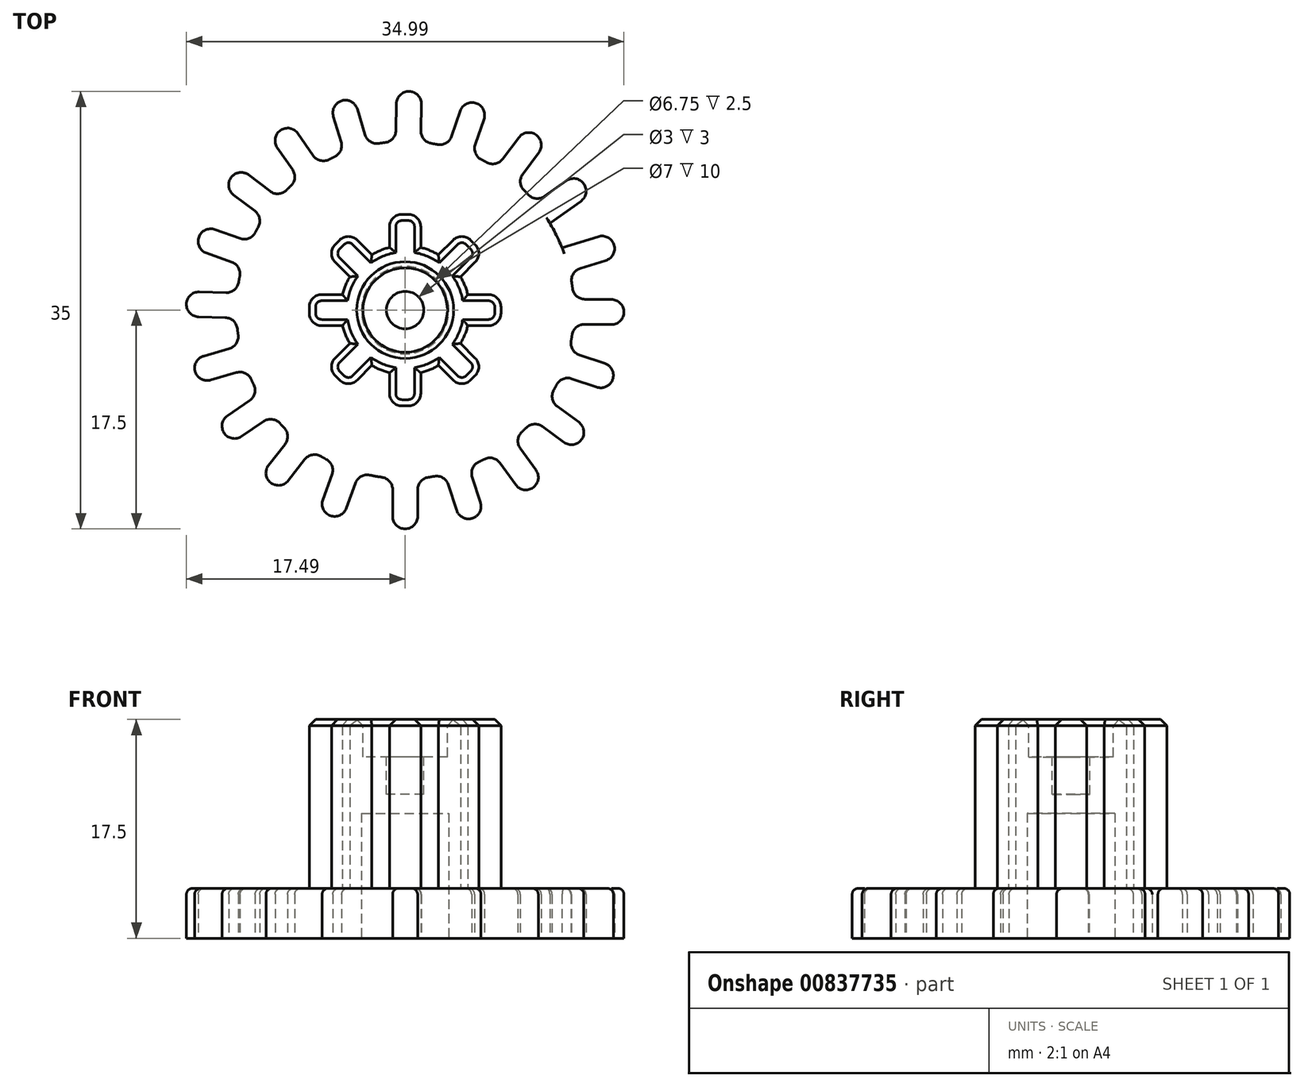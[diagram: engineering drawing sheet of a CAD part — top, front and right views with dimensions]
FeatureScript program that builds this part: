
annotation { "Feature Type Name" : "Feature", "Feature Type Description" : "" }
export const myFeature = defineFeature(function(context is Context, id is Id, definition is map)
    precondition{}
    {
        {
            var Q0;
            Q0=qCreatedBy(makeId("Top.planeOp"),FACE);
            var sketch = newSketch(context, id + "F0", { "sketchPlane" : qUnion([Q0])});
            skCircle(sketch, "E0", {"center": v(0, 0) * mm, "radius": 13.5 * mm});
            skSolve(sketch);
        }
        {
            var Q0;
            Q0 = qSketchRegion(id + "F0", true);
            extrude(context, id + "F1", {"entities" : qUnion([Q0]), "depth" : 4 * mm, "offsetDistance" : 25 * mm});
        }
        {
            var Q0;
            Q0=makeQuery(id+"F1.opExtrude","CAP_FACE",FACE,{"disambiguationData":[OSD([sQuery(id+"F0.wireOp",EDGE,"E0")])],"isStart":true});
            var sketch = newSketch(context, id + "F2", { "sketchPlane" : qUnion([Q0])});
            skCircle(sketch, "E1", {"center": v(0, 0) * mm, "radius": 5.17 * mm});
            skSolve(sketch);
        }
        {
            var Q0;
            Q0 = qSketchRegion(id + "F2", true);
            extrude(context, id + "F3", {"entities" : qUnion([Q0]), "operationType" : NewBodyOperationType.ADD, "oppositeDirection" : true, "depth" : 17.5 * mm, "offsetDistance" : 25 * mm});
        }
        {
            var Q0;
            Q0=makeQuery(id+"F1.opExtrude","CAP_FACE",FACE,{"disambiguationData":[OSD([sQuery(id+"F0.wireOp",EDGE,"E0")])],"isStart":true});
            var sketch = newSketch(context, id + "F4", { "sketchPlane" : qUnion([Q0])});
            skCircle(sketch, "E2", {"center": v(0, 0) * mm, "radius": 13.5 * mm});
            skLineSegment(sketch, "E3.bottom", {"start": v(1, 17.5) * mm, "end": v(-1, 17.5) * mm});
            skLineSegment(sketch, "E3.top", {"start": v(1, 9) * mm, "end": v(-1, 9) * mm});
            skLineSegment(sketch, "E3.left", {"start": v(1, 17.5) * mm, "end": v(1, 9) * mm});
            skLineSegment(sketch, "E3.right", {"start": v(-1, 17.5) * mm, "end": v(-1, 9) * mm});
            skPoint(sketch, "E3.middle", {"position": v(0, 13.25) * mm});
            skLineSegment(sketch, "E4.1.0", {"start": v(6.33, 16.35) * mm, "end": v(4.43, 16.96) * mm});
            skLineSegment(sketch, "E4.1.1", {"start": v(3.72, 8.26) * mm, "end": v(1.81, 8.87) * mm});
            skLineSegment(sketch, "E4.1.2", {"start": v(6.33, 16.35) * mm, "end": v(3.72, 8.26) * mm});
            skLineSegment(sketch, "E4.1.3", {"start": v(4.43, 16.96) * mm, "end": v(1.81, 8.87) * mm});
            skPoint(sketch, "E4.1.4", {"position": v(4.07, 12.6) * mm});
            skLineSegment(sketch, "E4.2.0", {"start": v(11.05, 13.61) * mm, "end": v(9.42, 14.78) * mm});
            skLineSegment(sketch, "E4.2.1", {"start": v(6.07, 6.72) * mm, "end": v(4.45, 7.89) * mm});
            skLineSegment(sketch, "E4.2.2", {"start": v(11.05, 13.61) * mm, "end": v(6.07, 6.72) * mm});
            skLineSegment(sketch, "E4.2.3", {"start": v(9.42, 14.78) * mm, "end": v(4.45, 7.89) * mm});
            skPoint(sketch, "E4.2.4", {"position": v(7.75, 10.75) * mm});
            skLineSegment(sketch, "E4.3.0", {"start": v(14.7, 9.56) * mm, "end": v(13.5, 11.17) * mm});
            skLineSegment(sketch, "E4.3.1", {"start": v(7.84, 4.52) * mm, "end": v(6.66, 6.14) * mm});
            skLineSegment(sketch, "E4.3.2", {"start": v(14.7, 9.56) * mm, "end": v(7.84, 4.52) * mm});
            skLineSegment(sketch, "E4.3.3", {"start": v(13.5, 11.17) * mm, "end": v(6.66, 6.14) * mm});
            skPoint(sketch, "E4.3.4", {"position": v(10.68, 7.85) * mm});
            skLineSegment(sketch, "E4.4.0", {"start": v(16.92, 4.58) * mm, "end": v(16.29, 6.48) * mm});
            skLineSegment(sketch, "E4.4.1", {"start": v(8.85, 1.9) * mm, "end": v(8.22, 3.8) * mm});
            skLineSegment(sketch, "E4.4.2", {"start": v(16.92, 4.58) * mm, "end": v(8.85, 1.9) * mm});
            skLineSegment(sketch, "E4.4.3", {"start": v(16.29, 6.48) * mm, "end": v(8.22, 3.8) * mm});
            skPoint(sketch, "E4.4.4", {"position": v(12.57, 4.19) * mm});
            skLineSegment(sketch, "E4.5.0", {"start": v(17.5, -0.84) * mm, "end": v(17.5, 1.16) * mm});
            skLineSegment(sketch, "E4.5.1", {"start": v(9, -0.92) * mm, "end": v(9, 1.08) * mm});
            skLineSegment(sketch, "E4.5.2", {"start": v(17.5, -0.84) * mm, "end": v(9, -0.92) * mm});
            skLineSegment(sketch, "E4.5.3", {"start": v(17.5, 1.16) * mm, "end": v(9, 1.08) * mm});
            skPoint(sketch, "E4.5.4", {"position": v(13.25, 0.12) * mm});
            skLineSegment(sketch, "E4.6.0", {"start": v(16.4, -6.18) * mm, "end": v(17, -4.27) * mm});
            skLineSegment(sketch, "E4.6.1", {"start": v(8.3, -3.64) * mm, "end": v(8.89, -1.73) * mm});
            skLineSegment(sketch, "E4.6.2", {"start": v(16.4, -6.18) * mm, "end": v(8.3, -3.64) * mm});
            skLineSegment(sketch, "E4.6.3", {"start": v(17, -4.27) * mm, "end": v(8.89, -1.73) * mm});
            skPoint(sketch, "E4.6.4", {"position": v(12.65, -3.96) * mm});
            skLineSegment(sketch, "E4.7.0", {"start": v(13.71, -10.92) * mm, "end": v(14.87, -9.29) * mm});
            skLineSegment(sketch, "E4.7.1", {"start": v(6.77, -6.01) * mm, "end": v(7.93, -4.38) * mm});
            skLineSegment(sketch, "E4.7.2", {"start": v(13.71, -10.92) * mm, "end": v(6.77, -6.01) * mm});
            skLineSegment(sketch, "E4.7.3", {"start": v(14.87, -9.29) * mm, "end": v(7.93, -4.38) * mm});
            skPoint(sketch, "E4.7.4", {"position": v(10.82, -7.65) * mm});
            skLineSegment(sketch, "E4.8.0", {"start": v(9.7, -14.6) * mm, "end": v(11.3, -13.4) * mm});
            skLineSegment(sketch, "E4.8.1", {"start": v(4.6, -7.8) * mm, "end": v(6.2, -6.6) * mm});
            skLineSegment(sketch, "E4.8.2", {"start": v(9.7, -14.6) * mm, "end": v(4.6, -7.8) * mm});
            skLineSegment(sketch, "E4.8.3", {"start": v(11.3, -13.4) * mm, "end": v(6.2, -6.6) * mm});
            skPoint(sketch, "E4.8.4", {"position": v(7.94, -10.6) * mm});
            skLineSegment(sketch, "E4.9.0", {"start": v(4.74, -16.88) * mm, "end": v(6.63, -16.23) * mm});
            skLineSegment(sketch, "E4.9.1", {"start": v(1.98, -8.84) * mm, "end": v(3.87, -8.19) * mm});
            skLineSegment(sketch, "E4.9.2", {"start": v(4.74, -16.88) * mm, "end": v(1.98, -8.84) * mm});
            skLineSegment(sketch, "E4.9.3", {"start": v(6.63, -16.23) * mm, "end": v(3.87, -8.19) * mm});
            skPoint(sketch, "E4.9.4", {"position": v(4.3, -12.53) * mm});
            skLineSegment(sketch, "E4.10.0", {"start": v(-0.68, -17.52) * mm, "end": v(1.32, -17.48) * mm});
            skLineSegment(sketch, "E4.10.1", {"start": v(-0.83, -9.02) * mm, "end": v(1.17, -8.98) * mm});
            skLineSegment(sketch, "E4.10.2", {"start": v(-0.68, -17.52) * mm, "end": v(-0.83, -9.02) * mm});
            skLineSegment(sketch, "E4.10.3", {"start": v(1.32, -17.48) * mm, "end": v(1.17, -8.98) * mm});
            skPoint(sketch, "E4.10.4", {"position": v(0.24, -13.25) * mm});
            skLineSegment(sketch, "E4.11.0", {"start": v(-6.03, -16.46) * mm, "end": v(-4.11, -17.04) * mm});
            skLineSegment(sketch, "E4.11.1", {"start": v(-3.56, -8.32) * mm, "end": v(-1.65, -8.9) * mm});
            skLineSegment(sketch, "E4.11.2", {"start": v(-6.03, -16.46) * mm, "end": v(-3.56, -8.32) * mm});
            skLineSegment(sketch, "E4.11.3", {"start": v(-4.11, -17.04) * mm, "end": v(-1.65, -8.9) * mm});
            skPoint(sketch, "E4.11.4", {"position": v(-3.84, -12.68) * mm});
            skLineSegment(sketch, "E4.12.0", {"start": v(-10.8, -13.81) * mm, "end": v(-9.15, -14.95) * mm});
            skLineSegment(sketch, "E4.12.1", {"start": v(-5.95, -6.83) * mm, "end": v(-4.3, -7.97) * mm});
            skLineSegment(sketch, "E4.12.2", {"start": v(-10.8, -13.81) * mm, "end": v(-5.95, -6.83) * mm});
            skLineSegment(sketch, "E4.12.3", {"start": v(-9.15, -14.95) * mm, "end": v(-4.3, -7.97) * mm});
            skPoint(sketch, "E4.12.4", {"position": v(-7.55, -10.89) * mm});
            skLineSegment(sketch, "E4.13.0", {"start": v(-14.52, -9.83) * mm, "end": v(-13.3, -11.42) * mm});
            skLineSegment(sketch, "E4.13.1", {"start": v(-7.76, -4.67) * mm, "end": v(-6.55, -6.26) * mm});
            skLineSegment(sketch, "E4.13.2", {"start": v(-14.52, -9.83) * mm, "end": v(-7.76, -4.67) * mm});
            skLineSegment(sketch, "E4.13.3", {"start": v(-13.3, -11.42) * mm, "end": v(-6.55, -6.26) * mm});
            skPoint(sketch, "E4.13.4", {"position": v(-10.53, -8.04) * mm});
            skLineSegment(sketch, "E4.14.0", {"start": v(-16.83, -4.9) * mm, "end": v(-16.17, -6.78) * mm});
            skLineSegment(sketch, "E4.14.1", {"start": v(-8.82, -2.06) * mm, "end": v(-8.15, -3.94) * mm});
            skLineSegment(sketch, "E4.14.2", {"start": v(-16.83, -4.9) * mm, "end": v(-8.82, -2.06) * mm});
            skLineSegment(sketch, "E4.14.3", {"start": v(-16.17, -6.78) * mm, "end": v(-8.15, -3.94) * mm});
            skPoint(sketch, "E4.14.4", {"position": v(-12.5, -4.42) * mm});
            skLineSegment(sketch, "E4.15.0", {"start": v(-17.52, 0.52) * mm, "end": v(-17.47, -1.48) * mm});
            skLineSegment(sketch, "E4.15.1", {"start": v(-9.02, 0.75) * mm, "end": v(-8.97, -1.25) * mm});
            skLineSegment(sketch, "E4.15.2", {"start": v(-17.52, 0.52) * mm, "end": v(-9.02, 0.75) * mm});
            skLineSegment(sketch, "E4.15.3", {"start": v(-17.47, -1.48) * mm, "end": v(-8.97, -1.25) * mm});
            skPoint(sketch, "E4.15.4", {"position": v(-13.24, -0.37) * mm});
            skLineSegment(sketch, "E4.16.0", {"start": v(-16.51, 5.88) * mm, "end": v(-17.08, 3.96) * mm});
            skLineSegment(sketch, "E4.16.1", {"start": v(-8.36, 3.49) * mm, "end": v(-8.92, 1.57) * mm});
            skLineSegment(sketch, "E4.16.2", {"start": v(-16.51, 5.88) * mm, "end": v(-8.36, 3.49) * mm});
            skLineSegment(sketch, "E4.16.3", {"start": v(-17.08, 3.96) * mm, "end": v(-8.92, 1.57) * mm});
            skPoint(sketch, "E4.16.4", {"position": v(-12.72, 3.72) * mm});
            skLineSegment(sketch, "E4.17.0", {"start": v(-13.9, 10.67) * mm, "end": v(-15.03, 9.01) * mm});
            skLineSegment(sketch, "E4.17.1", {"start": v(-6.88, 5.89) * mm, "end": v(-8, 4.23) * mm});
            skLineSegment(sketch, "E4.17.2", {"start": v(-13.9, 10.67) * mm, "end": v(-6.88, 5.89) * mm});
            skLineSegment(sketch, "E4.17.3", {"start": v(-15.03, 9.01) * mm, "end": v(-8, 4.23) * mm});
            skPoint(sketch, "E4.17.4", {"position": v(-10.96, 7.45) * mm});
            skLineSegment(sketch, "E4.18.0", {"start": v(-9.96, 14.42) * mm, "end": v(-11.54, 13.2) * mm});
            skLineSegment(sketch, "E4.18.1", {"start": v(-4.74, 7.72) * mm, "end": v(-6.32, 6.49) * mm});
            skLineSegment(sketch, "E4.18.2", {"start": v(-9.96, 14.42) * mm, "end": v(-4.74, 7.72) * mm});
            skLineSegment(sketch, "E4.18.3", {"start": v(-11.54, 13.2) * mm, "end": v(-6.32, 6.49) * mm});
            skPoint(sketch, "E4.18.4", {"position": v(-8.14, 10.46) * mm});
            skLineSegment(sketch, "E4.19.0", {"start": v(-5.05, 16.79) * mm, "end": v(-6.93, 16.1) * mm});
            skLineSegment(sketch, "E4.19.1", {"start": v(-2.14, 8.8) * mm, "end": v(-4.02, 8.12) * mm});
            skLineSegment(sketch, "E4.19.2", {"start": v(-5.05, 16.79) * mm, "end": v(-2.14, 8.8) * mm});
            skLineSegment(sketch, "E4.19.3", {"start": v(-6.93, 16.1) * mm, "end": v(-4.02, 8.12) * mm});
            skPoint(sketch, "E4.19.4", {"position": v(-4.53, 12.45) * mm});
            skLineSegment(sketch, "E4.anchor1", {"start": v(0, 0) * mm, "end": v(-1, 9) * mm, "construction": true});
            skLineSegment(sketch, "E4.anchor2", {"start": v(0, 0) * mm, "end": v(-4.02, 8.12) * mm, "construction": true});
            skSolve(sketch);
        }
        {
            var Q0;
            Q0 = qSketchRegion(id + "F4", true);
            extrude(context, id + "F5", {"entities" : qUnion([Q0]), "operationType" : NewBodyOperationType.ADD, "oppositeDirection" : true, "depth" : 4 * mm, "offsetDistance" : 25 * mm});
        }
        {
            var Q0;
            Q0=makeQuery(id+"F3.opExtrude","CAP_FACE",FACE,{"disambiguationData":[OSD([sQuery(id+"F2.wireOp",EDGE,"E1")])],"isStart":false});
            var sketch = newSketch(context, id + "F6", { "sketchPlane" : qUnion([Q0])});
            skLineSegment(sketch, "E5.bottom", {"start": v(7.66, -1.25) * mm, "end": v(2.67, -1.25) * mm});
            skLineSegment(sketch, "E5.top", {"start": v(7.67, 1.25) * mm, "end": v(2.67, 1.25) * mm});
            skLineSegment(sketch, "E5.left", {"start": v(7.67, -1.25) * mm, "end": v(7.67, 1.25) * mm});
            skLineSegment(sketch, "E5.right", {"start": v(2.67, -1.25) * mm, "end": v(2.67, 1.25) * mm});
            skPoint(sketch, "E5.middle", {"position": v(5.17, 0) * mm});
            skPoint(sketch, "E6.1.0", {"position": v(3.65, 3.65) * mm});
            skLineSegment(sketch, "E6.1.1", {"start": v(6.3, 4.54) * mm, "end": v(4.54, 6.3) * mm});
            skLineSegment(sketch, "E6.1.2", {"start": v(6.3, 4.54) * mm, "end": v(2.77, 1) * mm});
            skLineSegment(sketch, "E6.1.3", {"start": v(2.77, 1) * mm, "end": v(1, 2.77) * mm});
            skLineSegment(sketch, "E6.1.4", {"start": v(4.54, 6.3) * mm, "end": v(1, 2.77) * mm});
            skPoint(sketch, "E6.2.0", {"position": v(0, 5.17) * mm});
            skLineSegment(sketch, "E6.2.1", {"start": v(1.25, 7.67) * mm, "end": v(-1.25, 7.67) * mm});
            skLineSegment(sketch, "E6.2.2", {"start": v(1.25, 7.66) * mm, "end": v(1.25, 2.67) * mm});
            skLineSegment(sketch, "E6.2.3", {"start": v(1.25, 2.67) * mm, "end": v(-1.25, 2.67) * mm});
            skLineSegment(sketch, "E6.2.4", {"start": v(-1.25, 7.67) * mm, "end": v(-1.25, 2.67) * mm});
            skPoint(sketch, "E6.3.0", {"position": v(-3.65, 3.65) * mm});
            skLineSegment(sketch, "E6.3.1", {"start": v(-4.54, 6.3) * mm, "end": v(-6.3, 4.54) * mm});
            skLineSegment(sketch, "E6.3.2", {"start": v(-4.54, 6.3) * mm, "end": v(-1, 2.77) * mm});
            skLineSegment(sketch, "E6.3.3", {"start": v(-1, 2.77) * mm, "end": v(-2.77, 1) * mm});
            skLineSegment(sketch, "E6.3.4", {"start": v(-6.3, 4.54) * mm, "end": v(-2.77, 1) * mm});
            skPoint(sketch, "E6.4.0", {"position": v(-5.17, 0) * mm});
            skLineSegment(sketch, "E6.4.1", {"start": v(-7.67, 1.25) * mm, "end": v(-7.67, -1.25) * mm});
            skLineSegment(sketch, "E6.4.2", {"start": v(-7.66, 1.25) * mm, "end": v(-2.67, 1.25) * mm});
            skLineSegment(sketch, "E6.4.3", {"start": v(-2.67, 1.25) * mm, "end": v(-2.67, -1.25) * mm});
            skLineSegment(sketch, "E6.4.4", {"start": v(-7.67, -1.25) * mm, "end": v(-2.67, -1.25) * mm});
            skPoint(sketch, "E6.5.0", {"position": v(-3.65, -3.65) * mm});
            skLineSegment(sketch, "E6.5.1", {"start": v(-6.3, -4.54) * mm, "end": v(-4.54, -6.3) * mm});
            skLineSegment(sketch, "E6.5.2", {"start": v(-6.3, -4.54) * mm, "end": v(-2.77, -1) * mm});
            skLineSegment(sketch, "E6.5.3", {"start": v(-2.77, -1) * mm, "end": v(-1, -2.77) * mm});
            skLineSegment(sketch, "E6.5.4", {"start": v(-4.54, -6.3) * mm, "end": v(-1, -2.77) * mm});
            skPoint(sketch, "E6.6.0", {"position": v(0, -5.17) * mm});
            skLineSegment(sketch, "E6.6.1", {"start": v(-1.25, -7.67) * mm, "end": v(1.25, -7.67) * mm});
            skLineSegment(sketch, "E6.6.2", {"start": v(-1.25, -7.66) * mm, "end": v(-1.25, -2.67) * mm});
            skLineSegment(sketch, "E6.6.3", {"start": v(-1.25, -2.67) * mm, "end": v(1.25, -2.67) * mm});
            skLineSegment(sketch, "E6.6.4", {"start": v(1.25, -7.67) * mm, "end": v(1.25, -2.67) * mm});
            skPoint(sketch, "E6.7.0", {"position": v(3.65, -3.65) * mm});
            skLineSegment(sketch, "E6.7.1", {"start": v(4.54, -6.3) * mm, "end": v(6.3, -4.54) * mm});
            skLineSegment(sketch, "E6.7.2", {"start": v(4.54, -6.3) * mm, "end": v(1, -2.77) * mm});
            skLineSegment(sketch, "E6.7.3", {"start": v(1, -2.77) * mm, "end": v(2.77, -1) * mm});
            skLineSegment(sketch, "E6.7.4", {"start": v(6.3, -4.54) * mm, "end": v(2.77, -1) * mm});
            skPoint(sketch, "E6.center", {"position": v(0, 0) * mm});
            skSolve(sketch);
        }
        {
            var Q0;
            Q0 = qSketchRegion(id + "F6", true);
            extrude(context, id + "F7", {"entities" : qUnion([Q0]), "operationType" : NewBodyOperationType.ADD, "oppositeDirection" : true, "depth" : 14.7 * mm, "offsetDistance" : 25 * mm});
        }
        {
            var Q0;
            Q0=makeQuery(id+"F7.opExtrude","SWEPT_EDGE",EDGE,{"disambiguationData":[OSD([sQuery(id+"F6.wireOp",EDGE,"E6.6.1"),sQuery(id+"F6.wireOp",EDGE,"E6.6.4")])]});
            var Q1;
            Q1=makeQuery(id+"F7.opExtrude","SWEPT_EDGE",EDGE,{"disambiguationData":[OSD([sQuery(id+"F6.wireOp",EDGE,"E6.6.1"),sQuery(id+"F6.wireOp",EDGE,"E6.6.2")])]});
            var Q2;
            Q2=makeQuery(id+"F7.opExtrude","SWEPT_EDGE",EDGE,{"disambiguationData":[OSD([sQuery(id+"F6.wireOp",EDGE,"E6.5.1"),sQuery(id+"F6.wireOp",EDGE,"E6.5.4")])]});
            var Q3;
            Q3=makeQuery(id+"F7.opExtrude","SWEPT_EDGE",EDGE,{"disambiguationData":[OSD([sQuery(id+"F6.wireOp",EDGE,"E6.5.1"),sQuery(id+"F6.wireOp",EDGE,"E6.5.2")])]});
            var Q4;
            Q4=makeQuery(id+"F7.opExtrude","SWEPT_EDGE",EDGE,{"disambiguationData":[OSD([sQuery(id+"F6.wireOp",EDGE,"E6.4.1"),sQuery(id+"F6.wireOp",EDGE,"E6.4.4")])]});
            var Q5;
            Q5=makeQuery(id+"F7.opExtrude","SWEPT_EDGE",EDGE,{"disambiguationData":[OSD([sQuery(id+"F6.wireOp",EDGE,"E6.4.1"),sQuery(id+"F6.wireOp",EDGE,"E6.4.2")])]});
            var Q6;
            Q6=makeQuery(id+"F7.opExtrude","SWEPT_EDGE",EDGE,{"disambiguationData":[OSD([sQuery(id+"F6.wireOp",EDGE,"E6.3.1"),sQuery(id+"F6.wireOp",EDGE,"E6.3.4")])]});
            var Q7;
            Q7=makeQuery(id+"F7.opExtrude","SWEPT_EDGE",EDGE,{"disambiguationData":[OSD([sQuery(id+"F6.wireOp",EDGE,"E6.3.1"),sQuery(id+"F6.wireOp",EDGE,"E6.3.2")])]});
            var Q8;
            Q8=makeQuery(id+"F7.opExtrude","SWEPT_EDGE",EDGE,{"disambiguationData":[OSD([sQuery(id+"F6.wireOp",EDGE,"E6.2.1"),sQuery(id+"F6.wireOp",EDGE,"E6.2.4")])]});
            var Q9;
            Q9=makeQuery(id+"F7.opExtrude","SWEPT_EDGE",EDGE,{"disambiguationData":[OSD([sQuery(id+"F6.wireOp",EDGE,"E6.2.1"),sQuery(id+"F6.wireOp",EDGE,"E6.2.2")])]});
            var Q10;
            Q10=makeQuery(id+"F7.opExtrude","SWEPT_EDGE",EDGE,{"disambiguationData":[OSD([sQuery(id+"F6.wireOp",EDGE,"E6.1.1"),sQuery(id+"F6.wireOp",EDGE,"E6.1.4")])]});
            var Q11;
            Q11=makeQuery(id+"F7.opExtrude","SWEPT_EDGE",EDGE,{"disambiguationData":[OSD([sQuery(id+"F6.wireOp",EDGE,"E6.1.1"),sQuery(id+"F6.wireOp",EDGE,"E6.1.2")])]});
            var Q12;
            Q12=makeQuery(id+"F7.opExtrude","SWEPT_EDGE",EDGE,{"disambiguationData":[OSD([sQuery(id+"F6.wireOp",EDGE,"E5.top"),sQuery(id+"F6.wireOp",EDGE,"E5.left")])]});
            var Q13;
            Q13=makeQuery(id+"F7.opExtrude","SWEPT_EDGE",EDGE,{"disambiguationData":[OSD([sQuery(id+"F6.wireOp",EDGE,"E5.bottom"),sQuery(id+"F6.wireOp",EDGE,"E5.left")])]});
            var Q14;
            Q14=makeQuery(id+"F7.opExtrude","SWEPT_EDGE",EDGE,{"disambiguationData":[OSD([sQuery(id+"F6.wireOp",EDGE,"E6.7.1"),sQuery(id+"F6.wireOp",EDGE,"E6.7.4")])]});
            var Q15;
            Q15=makeQuery(id+"F7.opExtrude","SWEPT_EDGE",EDGE,{"disambiguationData":[OSD([sQuery(id+"F6.wireOp",EDGE,"E6.7.1"),sQuery(id+"F6.wireOp",EDGE,"E6.7.2")])]});
            fillet(context, id + "F8", {"entities" : qUnion([Q0, Q1, Q2, Q3, Q4, Q5, Q6, Q7, Q8, Q9, Q10, Q11, Q12, Q13, Q14, Q15]), "radius" : 1 * mm, "tangentPropagation" : true, "allowEdgeOverflow" : false});
        }
        {
            var Q0;
            Q0=makeQuery(id+"F7.boolean.opBoolean","MERGE",FACE,{"derivedFrom":[makeQuery(id+"F3.opExtrude","CAP_FACE",FACE,{"disambiguationData":[OSD([sQuery(id+"F2.wireOp",EDGE,"E1")])],"isStart":false}),makeQuery(id+"F7.opExtrude","CAP_FACE",FACE,{"disambiguationData":[OSD([sQuery(id+"F6.wireOp",EDGE,"E5.bottom"),sQuery(id+"F6.wireOp",EDGE,"E5.top"),sQuery(id+"F6.wireOp",EDGE,"E5.left"),sQuery(id+"F6.wireOp",EDGE,"E5.right"),sQuery(id+"F6.wireOp",EDGE,"E6.1.1"),sQuery(id+"F6.wireOp",EDGE,"E6.1.2"),sQuery(id+"F6.wireOp",EDGE,"E6.1.3"),sQuery(id+"F6.wireOp",EDGE,"E6.1.4"),sQuery(id+"F6.wireOp",EDGE,"E6.2.1"),sQuery(id+"F6.wireOp",EDGE,"E6.2.2"),sQuery(id+"F6.wireOp",EDGE,"E6.2.3"),sQuery(id+"F6.wireOp",EDGE,"E6.2.4"),sQuery(id+"F6.wireOp",EDGE,"E6.3.1"),sQuery(id+"F6.wireOp",EDGE,"E6.3.2"),sQuery(id+"F6.wireOp",EDGE,"E6.3.3"),sQuery(id+"F6.wireOp",EDGE,"E6.3.4"),sQuery(id+"F6.wireOp",EDGE,"E6.4.1"),sQuery(id+"F6.wireOp",EDGE,"E6.4.2"),sQuery(id+"F6.wireOp",EDGE,"E6.4.3"),sQuery(id+"F6.wireOp",EDGE,"E6.4.4"),sQuery(id+"F6.wireOp",EDGE,"E6.5.1"),sQuery(id+"F6.wireOp",EDGE,"E6.5.2"),sQuery(id+"F6.wireOp",EDGE,"E6.5.3"),sQuery(id+"F6.wireOp",EDGE,"E6.5.4"),sQuery(id+"F6.wireOp",EDGE,"E6.6.1"),sQuery(id+"F6.wireOp",EDGE,"E6.6.2"),sQuery(id+"F6.wireOp",EDGE,"E6.6.3"),sQuery(id+"F6.wireOp",EDGE,"E6.6.4"),sQuery(id+"F6.wireOp",EDGE,"E6.7.1"),sQuery(id+"F6.wireOp",EDGE,"E6.7.2"),sQuery(id+"F6.wireOp",EDGE,"E6.7.3"),sQuery(id+"F6.wireOp",EDGE,"E6.7.4")])],"isStart":true})]});
            var sketch = newSketch(context, id + "F9", { "sketchPlane" : qUnion([Q0])});
            skCircle(sketch, "E7", {"center": v(0, 0) * mm, "radius": 1.5 * mm});
            skSolve(sketch);
        }
        {
            var Q0;
            Q0 = qSketchRegion(id + "F9", true);
            extrude(context, id + "F10", {"entities" : qUnion([Q0]), "operationType" : NewBodyOperationType.REMOVE, "oppositeDirection" : true, "depth" : 6 * mm, "offsetDistance" : 25 * mm});
        }
        {
            var Q0;
            Q0=makeQuery(id+"F7.boolean.opBoolean","MERGE",FACE,{"derivedFrom":[makeQuery(id+"F3.opExtrude","CAP_FACE",FACE,{"disambiguationData":[OSD([sQuery(id+"F2.wireOp",EDGE,"E1")])],"isStart":false}),makeQuery(id+"F7.opExtrude","CAP_FACE",FACE,{"disambiguationData":[OSD([sQuery(id+"F6.wireOp",EDGE,"E5.bottom"),sQuery(id+"F6.wireOp",EDGE,"E5.top"),sQuery(id+"F6.wireOp",EDGE,"E5.left"),sQuery(id+"F6.wireOp",EDGE,"E5.right"),sQuery(id+"F6.wireOp",EDGE,"E6.1.1"),sQuery(id+"F6.wireOp",EDGE,"E6.1.2"),sQuery(id+"F6.wireOp",EDGE,"E6.1.3"),sQuery(id+"F6.wireOp",EDGE,"E6.1.4"),sQuery(id+"F6.wireOp",EDGE,"E6.2.1"),sQuery(id+"F6.wireOp",EDGE,"E6.2.2"),sQuery(id+"F6.wireOp",EDGE,"E6.2.3"),sQuery(id+"F6.wireOp",EDGE,"E6.2.4"),sQuery(id+"F6.wireOp",EDGE,"E6.3.1"),sQuery(id+"F6.wireOp",EDGE,"E6.3.2"),sQuery(id+"F6.wireOp",EDGE,"E6.3.3"),sQuery(id+"F6.wireOp",EDGE,"E6.3.4"),sQuery(id+"F6.wireOp",EDGE,"E6.4.1"),sQuery(id+"F6.wireOp",EDGE,"E6.4.2"),sQuery(id+"F6.wireOp",EDGE,"E6.4.3"),sQuery(id+"F6.wireOp",EDGE,"E6.4.4"),sQuery(id+"F6.wireOp",EDGE,"E6.5.1"),sQuery(id+"F6.wireOp",EDGE,"E6.5.2"),sQuery(id+"F6.wireOp",EDGE,"E6.5.3"),sQuery(id+"F6.wireOp",EDGE,"E6.5.4"),sQuery(id+"F6.wireOp",EDGE,"E6.6.1"),sQuery(id+"F6.wireOp",EDGE,"E6.6.2"),sQuery(id+"F6.wireOp",EDGE,"E6.6.3"),sQuery(id+"F6.wireOp",EDGE,"E6.6.4"),sQuery(id+"F6.wireOp",EDGE,"E6.7.1"),sQuery(id+"F6.wireOp",EDGE,"E6.7.2"),sQuery(id+"F6.wireOp",EDGE,"E6.7.3"),sQuery(id+"F6.wireOp",EDGE,"E6.7.4")])],"isStart":true})]});
            var sketch = newSketch(context, id + "F11", { "sketchPlane" : qUnion([Q0])});
            skCircle(sketch, "E8", {"center": v(0, 0) * mm, "radius": 3.38 * mm});
            skSolve(sketch);
        }
        {
            var Q0;
            Q0 = qSketchRegion(id + "F11", true);
            extrude(context, id + "F12", {"entities" : qUnion([Q0]), "operationType" : NewBodyOperationType.REMOVE, "oppositeDirection" : true, "depth" : 3 * mm, "offsetDistance" : 25 * mm});
        }
        {
            var Q0;
            Q0=makeQuery(id+"F5.boolean.opBoolean","MERGE",FACE,{"derivedFrom":[makeQuery(id+"F1.opExtrude","CAP_FACE",FACE,{"disambiguationData":[OSD([sQuery(id+"F0.wireOp",EDGE,"E0")])],"isStart":true}),makeQuery(id+"F5.opExtrude","CAP_FACE",FACE,{"disambiguationData":[OSD([sQuery(id+"F4.wireOp",EDGE,"E2"),sQuery(id+"F4.wireOp",EDGE,"E3.bottom"),sQuery(id+"F4.wireOp",EDGE,"E3.left"),sQuery(id+"F4.wireOp",EDGE,"E3.right"),sQuery(id+"F4.wireOp",EDGE,"E4.1.0"),sQuery(id+"F4.wireOp",EDGE,"E4.1.2"),sQuery(id+"F4.wireOp",EDGE,"E4.1.3"),sQuery(id+"F4.wireOp",EDGE,"E4.2.0"),sQuery(id+"F4.wireOp",EDGE,"E4.2.2"),sQuery(id+"F4.wireOp",EDGE,"E4.2.3"),sQuery(id+"F4.wireOp",EDGE,"E4.3.0"),sQuery(id+"F4.wireOp",EDGE,"E4.3.2"),sQuery(id+"F4.wireOp",EDGE,"E4.3.3"),sQuery(id+"F4.wireOp",EDGE,"E4.4.0"),sQuery(id+"F4.wireOp",EDGE,"E4.4.2"),sQuery(id+"F4.wireOp",EDGE,"E4.4.3"),sQuery(id+"F4.wireOp",EDGE,"E4.5.0"),sQuery(id+"F4.wireOp",EDGE,"E4.5.2"),sQuery(id+"F4.wireOp",EDGE,"E4.5.3"),sQuery(id+"F4.wireOp",EDGE,"E4.6.0"),sQuery(id+"F4.wireOp",EDGE,"E4.6.2"),sQuery(id+"F4.wireOp",EDGE,"E4.6.3"),sQuery(id+"F4.wireOp",EDGE,"E4.7.0"),sQuery(id+"F4.wireOp",EDGE,"E4.7.2"),sQuery(id+"F4.wireOp",EDGE,"E4.7.3"),sQuery(id+"F4.wireOp",EDGE,"E4.8.0"),sQuery(id+"F4.wireOp",EDGE,"E4.8.2"),sQuery(id+"F4.wireOp",EDGE,"E4.8.3"),sQuery(id+"F4.wireOp",EDGE,"E4.9.0"),sQuery(id+"F4.wireOp",EDGE,"E4.9.2"),sQuery(id+"F4.wireOp",EDGE,"E4.9.3"),sQuery(id+"F4.wireOp",EDGE,"E4.10.0"),sQuery(id+"F4.wireOp",EDGE,"E4.10.2"),sQuery(id+"F4.wireOp",EDGE,"E4.10.3"),sQuery(id+"F4.wireOp",EDGE,"E4.11.0"),sQuery(id+"F4.wireOp",EDGE,"E4.11.2"),sQuery(id+"F4.wireOp",EDGE,"E4.11.3"),sQuery(id+"F4.wireOp",EDGE,"E4.12.0"),sQuery(id+"F4.wireOp",EDGE,"E4.12.2"),sQuery(id+"F4.wireOp",EDGE,"E4.12.3"),sQuery(id+"F4.wireOp",EDGE,"E4.13.0"),sQuery(id+"F4.wireOp",EDGE,"E4.13.2"),sQuery(id+"F4.wireOp",EDGE,"E4.13.3"),sQuery(id+"F4.wireOp",EDGE,"E4.14.0"),sQuery(id+"F4.wireOp",EDGE,"E4.14.2"),sQuery(id+"F4.wireOp",EDGE,"E4.14.3"),sQuery(id+"F4.wireOp",EDGE,"E4.15.0"),sQuery(id+"F4.wireOp",EDGE,"E4.15.2"),sQuery(id+"F4.wireOp",EDGE,"E4.15.3"),sQuery(id+"F4.wireOp",EDGE,"E4.16.0"),sQuery(id+"F4.wireOp",EDGE,"E4.16.2"),sQuery(id+"F4.wireOp",EDGE,"E4.16.3"),sQuery(id+"F4.wireOp",EDGE,"E4.17.0"),sQuery(id+"F4.wireOp",EDGE,"E4.17.2"),sQuery(id+"F4.wireOp",EDGE,"E4.17.3"),sQuery(id+"F4.wireOp",EDGE,"E4.18.0"),sQuery(id+"F4.wireOp",EDGE,"E4.18.2"),sQuery(id+"F4.wireOp",EDGE,"E4.18.3"),sQuery(id+"F4.wireOp",EDGE,"E4.19.0"),sQuery(id+"F4.wireOp",EDGE,"E4.19.2"),sQuery(id+"F4.wireOp",EDGE,"E4.19.3")])],"isStart":true})]});
            var sketch = newSketch(context, id + "F13", { "sketchPlane" : qUnion([Q0])});
            skCircle(sketch, "E9", {"center": v(0, 0) * mm, "radius": 11.5 * mm});
            skCircle(sketch, "E10", {"center": v(0, 0) * mm, "radius": 5 * mm});
            skSolve(sketch);
        }
        {
            var Q0;
            Q0=makeQuery(id+"F13.imprint","IMPRINT",FACE,{"disambiguationData":[TD([[makeQuery(id+"F13.imprint","IMPRINT",EDGE,{"derivedFrom":sQuery(id+"F13.wireOp",EDGE,"E9")}),1.0]])]});
            extrude(context, id + "F14", {"entities" : qUnion([Q0]), "operationType" : NewBodyOperationType.REMOVE, "oppositeDirection" : true, "depth" : 2.25 * mm, "offsetDistance" : 25 * mm});
        }
        {
            var Q0;
            Q0=makeQuery(id+"F14.boolean.opBoolean","SPLIT",FACE,{"disambiguationData":[TD([makeQuery(id+"F14.opExtrude","SWEPT_FACE",FACE,{"disambiguationData":[OSD([sQuery(id+"F13.wireOp",EDGE,"E10")])]})])],"derivedFrom":makeQuery(id+"F5.boolean.opBoolean","MERGE",FACE,{"derivedFrom":[makeQuery(id+"F1.opExtrude","CAP_FACE",FACE,{"disambiguationData":[OSD([sQuery(id+"F0.wireOp",EDGE,"E0")])],"isStart":true}),makeQuery(id+"F5.opExtrude","CAP_FACE",FACE,{"disambiguationData":[OSD([sQuery(id+"F4.wireOp",EDGE,"E2"),sQuery(id+"F4.wireOp",EDGE,"E3.bottom"),sQuery(id+"F4.wireOp",EDGE,"E3.left"),sQuery(id+"F4.wireOp",EDGE,"E3.right"),sQuery(id+"F4.wireOp",EDGE,"E4.1.0"),sQuery(id+"F4.wireOp",EDGE,"E4.1.2"),sQuery(id+"F4.wireOp",EDGE,"E4.1.3"),sQuery(id+"F4.wireOp",EDGE,"E4.2.0"),sQuery(id+"F4.wireOp",EDGE,"E4.2.2"),sQuery(id+"F4.wireOp",EDGE,"E4.2.3"),sQuery(id+"F4.wireOp",EDGE,"E4.3.0"),sQuery(id+"F4.wireOp",EDGE,"E4.3.2"),sQuery(id+"F4.wireOp",EDGE,"E4.3.3"),sQuery(id+"F4.wireOp",EDGE,"E4.4.0"),sQuery(id+"F4.wireOp",EDGE,"E4.4.2"),sQuery(id+"F4.wireOp",EDGE,"E4.4.3"),sQuery(id+"F4.wireOp",EDGE,"E4.5.0"),sQuery(id+"F4.wireOp",EDGE,"E4.5.2"),sQuery(id+"F4.wireOp",EDGE,"E4.5.3"),sQuery(id+"F4.wireOp",EDGE,"E4.6.0"),sQuery(id+"F4.wireOp",EDGE,"E4.6.2"),sQuery(id+"F4.wireOp",EDGE,"E4.6.3"),sQuery(id+"F4.wireOp",EDGE,"E4.7.0"),sQuery(id+"F4.wireOp",EDGE,"E4.7.2"),sQuery(id+"F4.wireOp",EDGE,"E4.7.3"),sQuery(id+"F4.wireOp",EDGE,"E4.8.0"),sQuery(id+"F4.wireOp",EDGE,"E4.8.2"),sQuery(id+"F4.wireOp",EDGE,"E4.8.3"),sQuery(id+"F4.wireOp",EDGE,"E4.9.0"),sQuery(id+"F4.wireOp",EDGE,"E4.9.2"),sQuery(id+"F4.wireOp",EDGE,"E4.9.3"),sQuery(id+"F4.wireOp",EDGE,"E4.10.0"),sQuery(id+"F4.wireOp",EDGE,"E4.10.2"),sQuery(id+"F4.wireOp",EDGE,"E4.10.3"),sQuery(id+"F4.wireOp",EDGE,"E4.11.0"),sQuery(id+"F4.wireOp",EDGE,"E4.11.2"),sQuery(id+"F4.wireOp",EDGE,"E4.11.3"),sQuery(id+"F4.wireOp",EDGE,"E4.12.0"),sQuery(id+"F4.wireOp",EDGE,"E4.12.2"),sQuery(id+"F4.wireOp",EDGE,"E4.12.3"),sQuery(id+"F4.wireOp",EDGE,"E4.13.0"),sQuery(id+"F4.wireOp",EDGE,"E4.13.2"),sQuery(id+"F4.wireOp",EDGE,"E4.13.3"),sQuery(id+"F4.wireOp",EDGE,"E4.14.0"),sQuery(id+"F4.wireOp",EDGE,"E4.14.2"),sQuery(id+"F4.wireOp",EDGE,"E4.14.3"),sQuery(id+"F4.wireOp",EDGE,"E4.15.0"),sQuery(id+"F4.wireOp",EDGE,"E4.15.2"),sQuery(id+"F4.wireOp",EDGE,"E4.15.3"),sQuery(id+"F4.wireOp",EDGE,"E4.16.0"),sQuery(id+"F4.wireOp",EDGE,"E4.16.2"),sQuery(id+"F4.wireOp",EDGE,"E4.16.3"),sQuery(id+"F4.wireOp",EDGE,"E4.17.0"),sQuery(id+"F4.wireOp",EDGE,"E4.17.2"),sQuery(id+"F4.wireOp",EDGE,"E4.17.3"),sQuery(id+"F4.wireOp",EDGE,"E4.18.0"),sQuery(id+"F4.wireOp",EDGE,"E4.18.2"),sQuery(id+"F4.wireOp",EDGE,"E4.18.3"),sQuery(id+"F4.wireOp",EDGE,"E4.19.0"),sQuery(id+"F4.wireOp",EDGE,"E4.19.2"),sQuery(id+"F4.wireOp",EDGE,"E4.19.3")])],"isStart":true})]})});
            var sketch = newSketch(context, id + "F15", { "sketchPlane" : qUnion([Q0])});
            skCircle(sketch, "E11", {"center": v(0, 0) * mm, "radius": 3.5 * mm});
            skSolve(sketch);
        }
        {
            var Q0;
            Q0 = qSketchRegion(id + "F15", true);
            extrude(context, id + "F16", {"entities" : qUnion([Q0]), "operationType" : NewBodyOperationType.REMOVE, "oppositeDirection" : true, "depth" : 10 * mm, "offsetDistance" : 25 * mm});
        }
        {
            var Q0;
            Q0=makeQuery(id+"F14.boolean.opBoolean","COPY",FACE,{"derivedFrom":makeQuery(id+"F14.opExtrude","CAP_FACE",FACE,{"disambiguationData":[OSD([sQuery(id+"F13.wireOp",EDGE,"E9"),sQuery(id+"F13.wireOp",EDGE,"E10")])],"isStart":false})});
            extrude(context, id + "F17", {"entities" : qUnion([Q0]), "operationType" : NewBodyOperationType.ADD, "depth" : 2.25 * mm, "offsetDistance" : 25 * mm});
        }
        {
            var Q0;
            Q0=makeQuery(id+"F5.opExtrude","SWEPT_EDGE",EDGE,{"disambiguationData":[OSD([sQuery(id+"F4.wireOp",EDGE,"E4.3.0"),sQuery(id+"F4.wireOp",EDGE,"E4.3.2")])]});
            var Q1;
            Q1=makeQuery(id+"F5.opExtrude","SWEPT_EDGE",EDGE,{"disambiguationData":[OSD([sQuery(id+"F4.wireOp",EDGE,"E4.3.0"),sQuery(id+"F4.wireOp",EDGE,"E4.3.3")])]});
            var Q2;
            Q2=makeQuery(id+"F5.opExtrude","SWEPT_EDGE",EDGE,{"disambiguationData":[OSD([sQuery(id+"F4.wireOp",EDGE,"E4.4.0"),sQuery(id+"F4.wireOp",EDGE,"E4.4.3")])]});
            var Q3;
            Q3=makeQuery(id+"F5.opExtrude","SWEPT_EDGE",EDGE,{"disambiguationData":[OSD([sQuery(id+"F4.wireOp",EDGE,"E4.4.0"),sQuery(id+"F4.wireOp",EDGE,"E4.4.2")])]});
            var Q4;
            Q4=makeQuery(id+"F5.opExtrude","SWEPT_EDGE",EDGE,{"disambiguationData":[OSD([sQuery(id+"F4.wireOp",EDGE,"E4.5.0"),sQuery(id+"F4.wireOp",EDGE,"E4.5.3")])]});
            var Q5;
            Q5=makeQuery(id+"F5.opExtrude","SWEPT_EDGE",EDGE,{"disambiguationData":[OSD([sQuery(id+"F4.wireOp",EDGE,"E4.5.0"),sQuery(id+"F4.wireOp",EDGE,"E4.5.2")])]});
            var Q6;
            Q6=makeQuery(id+"F5.opExtrude","SWEPT_EDGE",EDGE,{"disambiguationData":[OSD([sQuery(id+"F4.wireOp",EDGE,"E4.6.0"),sQuery(id+"F4.wireOp",EDGE,"E4.6.3")])]});
            var Q7;
            Q7=makeQuery(id+"F5.opExtrude","SWEPT_EDGE",EDGE,{"disambiguationData":[OSD([sQuery(id+"F4.wireOp",EDGE,"E4.6.0"),sQuery(id+"F4.wireOp",EDGE,"E4.6.2")])]});
            var Q8;
            Q8=makeQuery(id+"F5.opExtrude","SWEPT_EDGE",EDGE,{"disambiguationData":[OSD([sQuery(id+"F4.wireOp",EDGE,"E4.7.0"),sQuery(id+"F4.wireOp",EDGE,"E4.7.3")])]});
            var Q9;
            Q9=makeQuery(id+"F5.opExtrude","SWEPT_EDGE",EDGE,{"disambiguationData":[OSD([sQuery(id+"F4.wireOp",EDGE,"E4.7.0"),sQuery(id+"F4.wireOp",EDGE,"E4.7.2")])]});
            var Q10;
            Q10=makeQuery(id+"F5.opExtrude","SWEPT_EDGE",EDGE,{"disambiguationData":[OSD([sQuery(id+"F4.wireOp",EDGE,"E4.8.0"),sQuery(id+"F4.wireOp",EDGE,"E4.8.3")])]});
            var Q11;
            Q11=makeQuery(id+"F5.opExtrude","SWEPT_EDGE",EDGE,{"disambiguationData":[OSD([sQuery(id+"F4.wireOp",EDGE,"E4.8.0"),sQuery(id+"F4.wireOp",EDGE,"E4.8.2")])]});
            var Q12;
            Q12=makeQuery(id+"F5.opExtrude","SWEPT_EDGE",EDGE,{"disambiguationData":[OSD([sQuery(id+"F4.wireOp",EDGE,"E4.9.0"),sQuery(id+"F4.wireOp",EDGE,"E4.9.3")])]});
            var Q13;
            Q13=makeQuery(id+"F5.opExtrude","SWEPT_EDGE",EDGE,{"disambiguationData":[OSD([sQuery(id+"F4.wireOp",EDGE,"E4.9.0"),sQuery(id+"F4.wireOp",EDGE,"E4.9.2")])]});
            var Q14;
            Q14=makeQuery(id+"F5.opExtrude","SWEPT_EDGE",EDGE,{"disambiguationData":[OSD([sQuery(id+"F4.wireOp",EDGE,"E4.10.0"),sQuery(id+"F4.wireOp",EDGE,"E4.10.3")])]});
            var Q15;
            Q15=makeQuery(id+"F5.opExtrude","SWEPT_EDGE",EDGE,{"disambiguationData":[OSD([sQuery(id+"F4.wireOp",EDGE,"E4.10.0"),sQuery(id+"F4.wireOp",EDGE,"E4.10.2")])]});
            var Q16;
            Q16=makeQuery(id+"F5.opExtrude","SWEPT_EDGE",EDGE,{"disambiguationData":[OSD([sQuery(id+"F4.wireOp",EDGE,"E4.11.0"),sQuery(id+"F4.wireOp",EDGE,"E4.11.3")])]});
            var Q17;
            Q17=makeQuery(id+"F5.opExtrude","SWEPT_EDGE",EDGE,{"disambiguationData":[OSD([sQuery(id+"F4.wireOp",EDGE,"E4.11.0"),sQuery(id+"F4.wireOp",EDGE,"E4.11.2")])]});
            var Q18;
            Q18=makeQuery(id+"F5.opExtrude","SWEPT_EDGE",EDGE,{"disambiguationData":[OSD([sQuery(id+"F4.wireOp",EDGE,"E4.12.0"),sQuery(id+"F4.wireOp",EDGE,"E4.12.3")])]});
            var Q19;
            Q19=makeQuery(id+"F5.opExtrude","SWEPT_EDGE",EDGE,{"disambiguationData":[OSD([sQuery(id+"F4.wireOp",EDGE,"E4.12.0"),sQuery(id+"F4.wireOp",EDGE,"E4.12.2")])]});
            var Q20;
            Q20=makeQuery(id+"F5.opExtrude","SWEPT_EDGE",EDGE,{"disambiguationData":[OSD([sQuery(id+"F4.wireOp",EDGE,"E4.13.0"),sQuery(id+"F4.wireOp",EDGE,"E4.13.3")])]});
            var Q21;
            Q21=makeQuery(id+"F5.opExtrude","SWEPT_EDGE",EDGE,{"disambiguationData":[OSD([sQuery(id+"F4.wireOp",EDGE,"E4.13.0"),sQuery(id+"F4.wireOp",EDGE,"E4.13.2")])]});
            var Q22;
            Q22=makeQuery(id+"F5.opExtrude","SWEPT_EDGE",EDGE,{"disambiguationData":[OSD([sQuery(id+"F4.wireOp",EDGE,"E4.14.0"),sQuery(id+"F4.wireOp",EDGE,"E4.14.3")])]});
            var Q23;
            Q23=makeQuery(id+"F5.opExtrude","SWEPT_EDGE",EDGE,{"disambiguationData":[OSD([sQuery(id+"F4.wireOp",EDGE,"E4.14.0"),sQuery(id+"F4.wireOp",EDGE,"E4.14.2")])]});
            var Q24;
            Q24=makeQuery(id+"F5.opExtrude","SWEPT_EDGE",EDGE,{"disambiguationData":[OSD([sQuery(id+"F4.wireOp",EDGE,"E4.15.0"),sQuery(id+"F4.wireOp",EDGE,"E4.15.3")])]});
            var Q25;
            Q25=makeQuery(id+"F5.opExtrude","SWEPT_EDGE",EDGE,{"disambiguationData":[OSD([sQuery(id+"F4.wireOp",EDGE,"E4.15.0"),sQuery(id+"F4.wireOp",EDGE,"E4.15.2")])]});
            var Q26;
            Q26=makeQuery(id+"F5.opExtrude","SWEPT_EDGE",EDGE,{"disambiguationData":[OSD([sQuery(id+"F4.wireOp",EDGE,"E4.16.0"),sQuery(id+"F4.wireOp",EDGE,"E4.16.3")])]});
            var Q27;
            Q27=makeQuery(id+"F5.opExtrude","SWEPT_EDGE",EDGE,{"disambiguationData":[OSD([sQuery(id+"F4.wireOp",EDGE,"E4.16.0"),sQuery(id+"F4.wireOp",EDGE,"E4.16.2")])]});
            var Q28;
            Q28=makeQuery(id+"F5.opExtrude","SWEPT_EDGE",EDGE,{"disambiguationData":[OSD([sQuery(id+"F4.wireOp",EDGE,"E4.17.0"),sQuery(id+"F4.wireOp",EDGE,"E4.17.3")])]});
            var Q29;
            Q29=makeQuery(id+"F5.opExtrude","SWEPT_EDGE",EDGE,{"disambiguationData":[OSD([sQuery(id+"F4.wireOp",EDGE,"E4.17.0"),sQuery(id+"F4.wireOp",EDGE,"E4.17.2")])]});
            var Q30;
            Q30=makeQuery(id+"F5.opExtrude","SWEPT_EDGE",EDGE,{"disambiguationData":[OSD([sQuery(id+"F4.wireOp",EDGE,"E4.18.0"),sQuery(id+"F4.wireOp",EDGE,"E4.18.3")])]});
            var Q31;
            Q31=makeQuery(id+"F5.opExtrude","SWEPT_EDGE",EDGE,{"disambiguationData":[OSD([sQuery(id+"F4.wireOp",EDGE,"E4.18.0"),sQuery(id+"F4.wireOp",EDGE,"E4.18.2")])]});
            var Q32;
            Q32=makeQuery(id+"F5.opExtrude","SWEPT_EDGE",EDGE,{"disambiguationData":[OSD([sQuery(id+"F4.wireOp",EDGE,"E4.19.0"),sQuery(id+"F4.wireOp",EDGE,"E4.19.3")])]});
            var Q33;
            Q33=makeQuery(id+"F5.opExtrude","SWEPT_EDGE",EDGE,{"disambiguationData":[OSD([sQuery(id+"F4.wireOp",EDGE,"E4.19.0"),sQuery(id+"F4.wireOp",EDGE,"E4.19.2")])]});
            var Q34;
            Q34=makeQuery(id+"F5.opExtrude","SWEPT_EDGE",EDGE,{"disambiguationData":[OSD([sQuery(id+"F4.wireOp",EDGE,"E3.bottom"),sQuery(id+"F4.wireOp",EDGE,"E3.right")])]});
            var Q35;
            Q35=makeQuery(id+"F5.opExtrude","SWEPT_EDGE",EDGE,{"disambiguationData":[OSD([sQuery(id+"F4.wireOp",EDGE,"E3.bottom"),sQuery(id+"F4.wireOp",EDGE,"E3.left")])]});
            var Q36;
            Q36=makeQuery(id+"F5.opExtrude","SWEPT_EDGE",EDGE,{"disambiguationData":[OSD([sQuery(id+"F4.wireOp",EDGE,"E4.1.0"),sQuery(id+"F4.wireOp",EDGE,"E4.1.3")])]});
            var Q37;
            Q37=makeQuery(id+"F5.opExtrude","SWEPT_EDGE",EDGE,{"disambiguationData":[OSD([sQuery(id+"F4.wireOp",EDGE,"E4.1.0"),sQuery(id+"F4.wireOp",EDGE,"E4.1.2")])]});
            var Q38;
            Q38=makeQuery(id+"F5.opExtrude","SWEPT_EDGE",EDGE,{"disambiguationData":[OSD([sQuery(id+"F4.wireOp",EDGE,"E4.2.0"),sQuery(id+"F4.wireOp",EDGE,"E4.2.2")])]});
            var Q39;
            Q39=makeQuery(id+"F5.opExtrude","SWEPT_EDGE",EDGE,{"disambiguationData":[OSD([sQuery(id+"F4.wireOp",EDGE,"E4.2.0"),sQuery(id+"F4.wireOp",EDGE,"E4.2.3")])]});
            fillet(context, id + "F18", {"entities" : qUnion([Q0, Q1, Q2, Q3, Q4, Q5, Q6, Q7, Q8, Q9, Q10, Q11, Q12, Q13, Q14, Q15, Q16, Q17, Q18, Q19, Q20, Q21, Q22, Q23, Q24, Q25, Q26, Q27, Q28, Q29, Q30, Q31, Q32, Q33, Q34, Q35, Q36, Q37, Q38, Q39]), "radius" : 1 * mm, "tangentPropagation" : true, "allowEdgeOverflow" : false});
        }
        {
            var Q0;
            Q0=makeQuery(id+"F5.opExtrude","SWEPT_EDGE",EDGE,{"disambiguationData":[OSD([sQuery(id+"F4.wireOp",EDGE,"E2"),sQuery(id+"F4.wireOp",EDGE,"E4.7.2")])]});
            var Q1;
            Q1=makeQuery(id+"F5.opExtrude","SWEPT_EDGE",EDGE,{"disambiguationData":[OSD([sQuery(id+"F4.wireOp",EDGE,"E2"),sQuery(id+"F4.wireOp",EDGE,"E4.8.3")])]});
            var Q2;
            Q2=makeQuery(id+"F5.opExtrude","SWEPT_EDGE",EDGE,{"disambiguationData":[OSD([sQuery(id+"F4.wireOp",EDGE,"E2"),sQuery(id+"F4.wireOp",EDGE,"E4.8.2")])]});
            var Q3;
            Q3=makeQuery(id+"F5.opExtrude","SWEPT_EDGE",EDGE,{"disambiguationData":[OSD([sQuery(id+"F4.wireOp",EDGE,"E2"),sQuery(id+"F4.wireOp",EDGE,"E4.9.3")])]});
            var Q4;
            Q4=makeQuery(id+"F5.opExtrude","SWEPT_EDGE",EDGE,{"disambiguationData":[OSD([sQuery(id+"F4.wireOp",EDGE,"E2"),sQuery(id+"F4.wireOp",EDGE,"E4.9.2")])]});
            var Q5;
            Q5=makeQuery(id+"F5.opExtrude","SWEPT_EDGE",EDGE,{"disambiguationData":[OSD([sQuery(id+"F4.wireOp",EDGE,"E2"),sQuery(id+"F4.wireOp",EDGE,"E4.10.3")])]});
            var Q6;
            Q6=makeQuery(id+"F5.opExtrude","SWEPT_EDGE",EDGE,{"disambiguationData":[OSD([sQuery(id+"F4.wireOp",EDGE,"E2"),sQuery(id+"F4.wireOp",EDGE,"E4.12.3")])]});
            var Q7;
            Q7=makeQuery(id+"F5.opExtrude","SWEPT_EDGE",EDGE,{"disambiguationData":[OSD([sQuery(id+"F4.wireOp",EDGE,"E2"),sQuery(id+"F4.wireOp",EDGE,"E4.10.2")])]});
            var Q8;
            Q8=makeQuery(id+"F5.opExtrude","SWEPT_EDGE",EDGE,{"disambiguationData":[OSD([sQuery(id+"F4.wireOp",EDGE,"E2"),sQuery(id+"F4.wireOp",EDGE,"E4.11.2")])]});
            var Q9;
            Q9=makeQuery(id+"F5.opExtrude","SWEPT_EDGE",EDGE,{"disambiguationData":[OSD([sQuery(id+"F4.wireOp",EDGE,"E2"),sQuery(id+"F4.wireOp",EDGE,"E4.11.3")])]});
            var Q10;
            Q10=makeQuery(id+"F5.opExtrude","SWEPT_EDGE",EDGE,{"disambiguationData":[OSD([sQuery(id+"F4.wireOp",EDGE,"E2"),sQuery(id+"F4.wireOp",EDGE,"E4.13.3")])]});
            var Q11;
            Q11=makeQuery(id+"F5.opExtrude","SWEPT_EDGE",EDGE,{"disambiguationData":[OSD([sQuery(id+"F4.wireOp",EDGE,"E2"),sQuery(id+"F4.wireOp",EDGE,"E4.12.2")])]});
            var Q12;
            Q12=makeQuery(id+"F5.opExtrude","SWEPT_EDGE",EDGE,{"disambiguationData":[OSD([sQuery(id+"F4.wireOp",EDGE,"E2"),sQuery(id+"F4.wireOp",EDGE,"E4.13.2")])]});
            var Q13;
            Q13=makeQuery(id+"F5.opExtrude","SWEPT_EDGE",EDGE,{"disambiguationData":[OSD([sQuery(id+"F4.wireOp",EDGE,"E2"),sQuery(id+"F4.wireOp",EDGE,"E4.14.3")])]});
            var Q14;
            Q14=makeQuery(id+"F5.opExtrude","SWEPT_EDGE",EDGE,{"disambiguationData":[OSD([sQuery(id+"F4.wireOp",EDGE,"E2"),sQuery(id+"F4.wireOp",EDGE,"E4.14.2")])]});
            var Q15;
            Q15=makeQuery(id+"F5.opExtrude","SWEPT_EDGE",EDGE,{"disambiguationData":[OSD([sQuery(id+"F4.wireOp",EDGE,"E2"),sQuery(id+"F4.wireOp",EDGE,"E4.15.3")])]});
            var Q16;
            Q16=makeQuery(id+"F5.opExtrude","SWEPT_EDGE",EDGE,{"disambiguationData":[OSD([sQuery(id+"F4.wireOp",EDGE,"E2"),sQuery(id+"F4.wireOp",EDGE,"E4.15.2")])]});
            var Q17;
            Q17=makeQuery(id+"F5.opExtrude","SWEPT_EDGE",EDGE,{"disambiguationData":[OSD([sQuery(id+"F4.wireOp",EDGE,"E2"),sQuery(id+"F4.wireOp",EDGE,"E4.16.2")])]});
            var Q18;
            Q18=makeQuery(id+"F5.opExtrude","SWEPT_EDGE",EDGE,{"disambiguationData":[OSD([sQuery(id+"F4.wireOp",EDGE,"E2"),sQuery(id+"F4.wireOp",EDGE,"E4.16.3")])]});
            var Q19;
            Q19=makeQuery(id+"F5.opExtrude","SWEPT_EDGE",EDGE,{"disambiguationData":[OSD([sQuery(id+"F4.wireOp",EDGE,"E2"),sQuery(id+"F4.wireOp",EDGE,"E4.17.3")])]});
            var Q20;
            Q20=makeQuery(id+"F5.opExtrude","SWEPT_EDGE",EDGE,{"disambiguationData":[OSD([sQuery(id+"F4.wireOp",EDGE,"E2"),sQuery(id+"F4.wireOp",EDGE,"E4.17.2")])]});
            var Q21;
            Q21=makeQuery(id+"F5.opExtrude","SWEPT_EDGE",EDGE,{"disambiguationData":[OSD([sQuery(id+"F4.wireOp",EDGE,"E2"),sQuery(id+"F4.wireOp",EDGE,"E4.18.3")])]});
            var Q22;
            Q22=makeQuery(id+"F5.opExtrude","SWEPT_EDGE",EDGE,{"disambiguationData":[OSD([sQuery(id+"F4.wireOp",EDGE,"E2"),sQuery(id+"F4.wireOp",EDGE,"E4.18.2")])]});
            var Q23;
            Q23=makeQuery(id+"F5.opExtrude","SWEPT_EDGE",EDGE,{"disambiguationData":[OSD([sQuery(id+"F4.wireOp",EDGE,"E2"),sQuery(id+"F4.wireOp",EDGE,"E4.19.2")])]});
            var Q24;
            Q24=makeQuery(id+"F5.opExtrude","SWEPT_EDGE",EDGE,{"disambiguationData":[OSD([sQuery(id+"F4.wireOp",EDGE,"E2"),sQuery(id+"F4.wireOp",EDGE,"E3.right")])]});
            var Q25;
            Q25=makeQuery(id+"F5.opExtrude","SWEPT_EDGE",EDGE,{"disambiguationData":[OSD([sQuery(id+"F4.wireOp",EDGE,"E2"),sQuery(id+"F4.wireOp",EDGE,"E3.left")])]});
            var Q26;
            Q26=makeQuery(id+"F5.opExtrude","SWEPT_EDGE",EDGE,{"disambiguationData":[OSD([sQuery(id+"F4.wireOp",EDGE,"E2"),sQuery(id+"F4.wireOp",EDGE,"E4.1.2")])]});
            var Q27;
            Q27=makeQuery(id+"F5.opExtrude","SWEPT_EDGE",EDGE,{"disambiguationData":[OSD([sQuery(id+"F4.wireOp",EDGE,"E2"),sQuery(id+"F4.wireOp",EDGE,"E4.2.3")])]});
            var Q28;
            Q28=makeQuery(id+"F5.opExtrude","SWEPT_EDGE",EDGE,{"disambiguationData":[OSD([sQuery(id+"F4.wireOp",EDGE,"E2"),sQuery(id+"F4.wireOp",EDGE,"E4.1.3")])]});
            var Q29;
            Q29=makeQuery(id+"F5.opExtrude","SWEPT_EDGE",EDGE,{"disambiguationData":[OSD([sQuery(id+"F4.wireOp",EDGE,"E2"),sQuery(id+"F4.wireOp",EDGE,"E4.2.2")])]});
            var Q30;
            Q30=makeQuery(id+"F5.opExtrude","SWEPT_EDGE",EDGE,{"disambiguationData":[OSD([sQuery(id+"F4.wireOp",EDGE,"E2"),sQuery(id+"F4.wireOp",EDGE,"E4.3.3")])]});
            var Q31;
            Q31=makeQuery(id+"F5.opExtrude","SWEPT_EDGE",EDGE,{"disambiguationData":[OSD([sQuery(id+"F4.wireOp",EDGE,"E2"),sQuery(id+"F4.wireOp",EDGE,"E4.3.2")])]});
            var Q32;
            Q32=makeQuery(id+"F5.opExtrude","SWEPT_EDGE",EDGE,{"disambiguationData":[OSD([sQuery(id+"F4.wireOp",EDGE,"E2"),sQuery(id+"F4.wireOp",EDGE,"E4.4.3")])]});
            var Q33;
            Q33=makeQuery(id+"F5.opExtrude","SWEPT_EDGE",EDGE,{"disambiguationData":[OSD([sQuery(id+"F4.wireOp",EDGE,"E2"),sQuery(id+"F4.wireOp",EDGE,"E4.4.2")])]});
            var Q34;
            Q34=makeQuery(id+"F5.opExtrude","SWEPT_EDGE",EDGE,{"disambiguationData":[OSD([sQuery(id+"F4.wireOp",EDGE,"E2"),sQuery(id+"F4.wireOp",EDGE,"E4.7.3")])]});
            var Q35;
            Q35=makeQuery(id+"F5.opExtrude","SWEPT_EDGE",EDGE,{"disambiguationData":[OSD([sQuery(id+"F4.wireOp",EDGE,"E2"),sQuery(id+"F4.wireOp",EDGE,"E4.6.3")])]});
            var Q36;
            Q36=makeQuery(id+"F5.opExtrude","SWEPT_EDGE",EDGE,{"disambiguationData":[OSD([sQuery(id+"F4.wireOp",EDGE,"E2"),sQuery(id+"F4.wireOp",EDGE,"E4.5.2")])]});
            var Q37;
            Q37=makeQuery(id+"F5.opExtrude","SWEPT_EDGE",EDGE,{"disambiguationData":[OSD([sQuery(id+"F4.wireOp",EDGE,"E2"),sQuery(id+"F4.wireOp",EDGE,"E4.5.3")])]});
            var Q38;
            Q38=makeQuery(id+"F5.opExtrude","SWEPT_EDGE",EDGE,{"disambiguationData":[OSD([sQuery(id+"F4.wireOp",EDGE,"E2"),sQuery(id+"F4.wireOp",EDGE,"E4.6.2")])]});
            var Q39;
            Q39=makeQuery(id+"F5.opExtrude","SWEPT_EDGE",EDGE,{"disambiguationData":[OSD([sQuery(id+"F4.wireOp",EDGE,"E2"),sQuery(id+"F4.wireOp",EDGE,"E4.19.3")])]});
            fillet(context, id + "F19", {"entities" : qUnion([Q0, Q1, Q2, Q3, Q4, Q5, Q6, Q7, Q8, Q9, Q10, Q11, Q12, Q13, Q14, Q15, Q16, Q17, Q18, Q19, Q20, Q21, Q22, Q23, Q24, Q25, Q26, Q27, Q28, Q29, Q30, Q31, Q32, Q33, Q34, Q35, Q36, Q37, Q38, Q39]), "radius" : 1 * mm, "tangentPropagation" : true, "allowEdgeOverflow" : false});
        }
        {
            var Q0;
            Q0=makeQuery(id+"F7.boolean.opBoolean","MERGE",FACE,{"derivedFrom":[makeQuery(id+"F3.opExtrude","CAP_FACE",FACE,{"disambiguationData":[OSD([sQuery(id+"F2.wireOp",EDGE,"E1")])],"isStart":false}),makeQuery(id+"F7.opExtrude","CAP_FACE",FACE,{"disambiguationData":[OSD([sQuery(id+"F6.wireOp",EDGE,"E5.bottom"),sQuery(id+"F6.wireOp",EDGE,"E5.top"),sQuery(id+"F6.wireOp",EDGE,"E5.left"),sQuery(id+"F6.wireOp",EDGE,"E5.right"),sQuery(id+"F6.wireOp",EDGE,"E6.1.1"),sQuery(id+"F6.wireOp",EDGE,"E6.1.2"),sQuery(id+"F6.wireOp",EDGE,"E6.1.3"),sQuery(id+"F6.wireOp",EDGE,"E6.1.4"),sQuery(id+"F6.wireOp",EDGE,"E6.2.1"),sQuery(id+"F6.wireOp",EDGE,"E6.2.2"),sQuery(id+"F6.wireOp",EDGE,"E6.2.3"),sQuery(id+"F6.wireOp",EDGE,"E6.2.4"),sQuery(id+"F6.wireOp",EDGE,"E6.3.1"),sQuery(id+"F6.wireOp",EDGE,"E6.3.2"),sQuery(id+"F6.wireOp",EDGE,"E6.3.3"),sQuery(id+"F6.wireOp",EDGE,"E6.3.4"),sQuery(id+"F6.wireOp",EDGE,"E6.4.1"),sQuery(id+"F6.wireOp",EDGE,"E6.4.2"),sQuery(id+"F6.wireOp",EDGE,"E6.4.3"),sQuery(id+"F6.wireOp",EDGE,"E6.4.4"),sQuery(id+"F6.wireOp",EDGE,"E6.5.1"),sQuery(id+"F6.wireOp",EDGE,"E6.5.2"),sQuery(id+"F6.wireOp",EDGE,"E6.5.3"),sQuery(id+"F6.wireOp",EDGE,"E6.5.4"),sQuery(id+"F6.wireOp",EDGE,"E6.6.1"),sQuery(id+"F6.wireOp",EDGE,"E6.6.2"),sQuery(id+"F6.wireOp",EDGE,"E6.6.3"),sQuery(id+"F6.wireOp",EDGE,"E6.6.4"),sQuery(id+"F6.wireOp",EDGE,"E6.7.1"),sQuery(id+"F6.wireOp",EDGE,"E6.7.2"),sQuery(id+"F6.wireOp",EDGE,"E6.7.3"),sQuery(id+"F6.wireOp",EDGE,"E6.7.4")])],"isStart":true})]});
            chamfer(context, id + "F20", {"entities" : qUnion([Q0]), "width" : .5 * mm, "tangentPropagation" : true});
        }
        {
            var Q0;
            Q0=makeQuery(id+"F5.opExtrude","CAP_EDGE",EDGE,{"disambiguationData":[OSD([sQuery(id+"F4.wireOp",EDGE,"E4.2.2")])],"isStart":false});
            fillet(context, id + "F21", {"entities" : qUnion([Q0]), "radius" : .5 * mm, "tangentPropagation" : true, "allowEdgeOverflow" : false});
        }
    });
